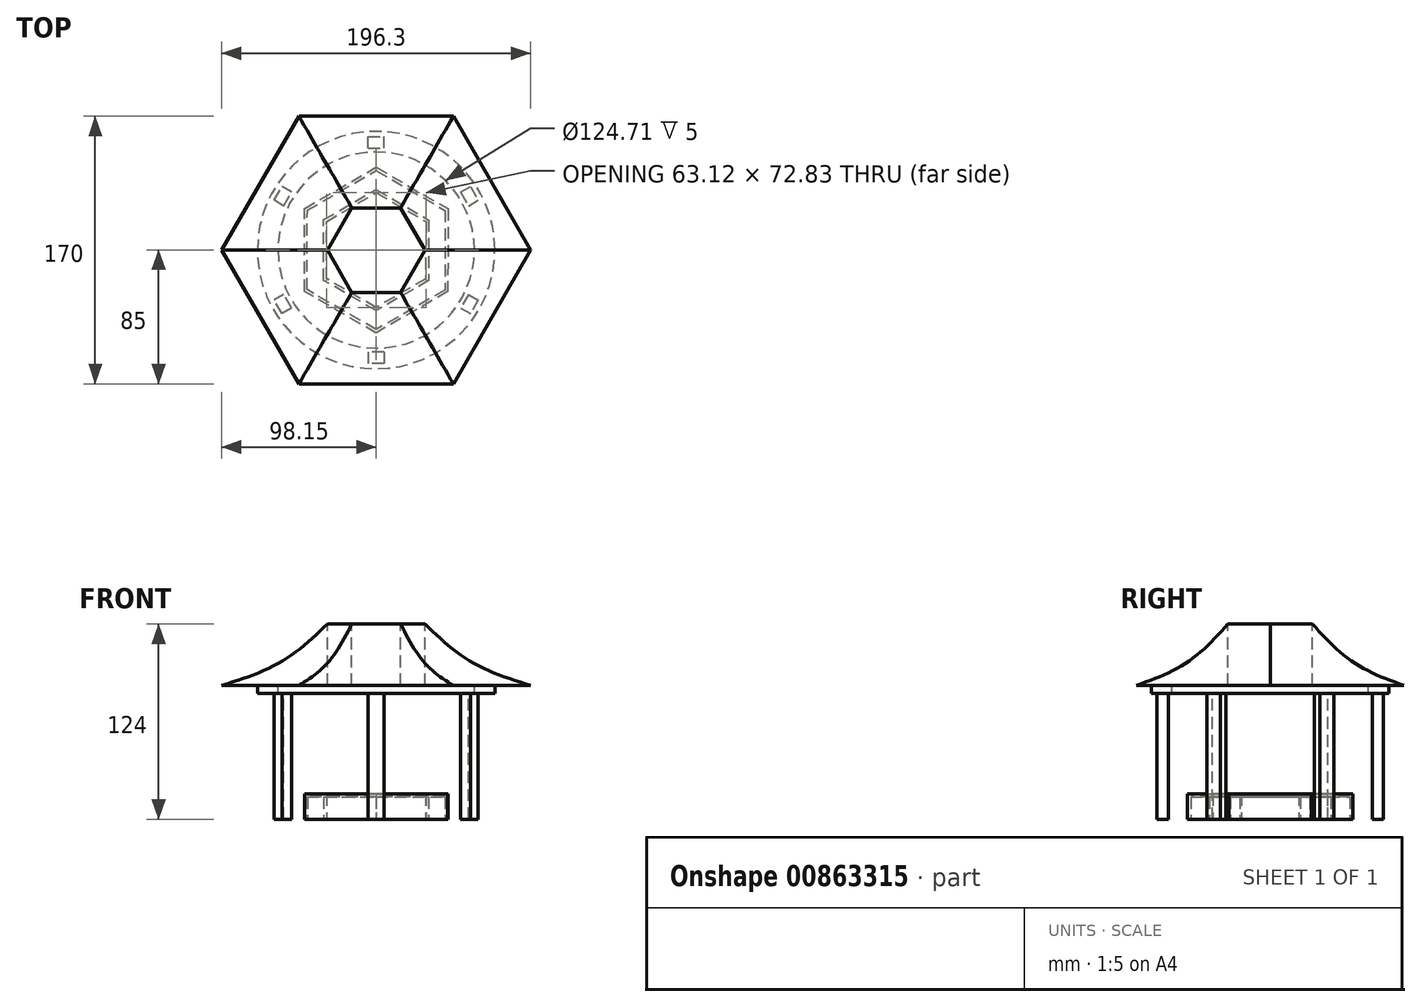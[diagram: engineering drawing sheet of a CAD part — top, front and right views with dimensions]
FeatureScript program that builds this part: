
annotation { "Feature Type Name" : "Feature", "Feature Type Description" : "" }
export const myFeature = defineFeature(function(context is Context, id is Id, definition is map)
    precondition{}
    {
        {
            var Q0;
            Q0=qCreatedBy(makeId("Top.planeOp"),FACE);
            var sketch = newSketch(context, id + "F0", { "sketchPlane" : qUnion([Q0])});
            skCircle(sketch, "E0.cCircle", {"center": v(0, 0) * mm, "radius": 85 * mm, "construction": true});
            skLineSegment(sketch, "E0.0", {"start": v(-49.07, 85) * mm, "end": v(49.07, 85) * mm});
            skLineSegment(sketch, "E0.1", {"start": v(49.07, 85) * mm, "end": v(98.15, 0) * mm});
            skLineSegment(sketch, "E0.2", {"start": v(98.15, 0) * mm, "end": v(49.07, -85) * mm});
            skLineSegment(sketch, "E0.3", {"start": v(49.07, -85) * mm, "end": v(-49.07, -85) * mm});
            skLineSegment(sketch, "E0.4", {"start": v(-49.07, -85) * mm, "end": v(-98.15, 0) * mm});
            skLineSegment(sketch, "E0.5", {"start": v(-98.15, 0) * mm, "end": v(-49.07, 85) * mm});
            skPoint(sketch, "E0.0.midPoint", {"position": v(0, 85) * mm});
            skSolve(sketch);
        }
        {
            var Q0;
            Q0=qCreatedBy(makeId("Top.planeOp"),FACE);
            cPlane(context, id + "F1", {"entities" : qUnion([Q0]), "cplaneType" : CPlaneType.OFFSET, "offset" : 39 * mm, "width" : 150 * mm, "height" : 150 * mm});
        }
        {
            var Q0;
            Q0=qCreatedBy(id+"F1.planeOp",FACE);
            var sketch = newSketch(context, id + "F2", { "sketchPlane" : qUnion([Q0])});
            skLineSegment(sketch, "E1.0", {"start": v(-98.15, 0) * mm, "end": v(-49.07, 85) * mm});
            skLineSegment(sketch, "E1.1", {"start": v(-49.07, 85) * mm, "end": v(49.07, 85) * mm});
            skLineSegment(sketch, "E1.2", {"start": v(49.07, 85) * mm, "end": v(98.15, 0) * mm});
            skLineSegment(sketch, "E1.3", {"start": v(98.15, 0) * mm, "end": v(49.07, -85) * mm});
            skLineSegment(sketch, "E1.4", {"start": v(49.07, -85) * mm, "end": v(-49.07, -85) * mm});
            skLineSegment(sketch, "E1.5", {"start": v(-49.07, -85) * mm, "end": v(-98.15, 0) * mm});
            skLineSegment(sketch, "E2.0", {"start": v(-15.47, -26.8) * mm, "end": v(-30.95, 0) * mm});
            skLineSegment(sketch, "E2.1", {"start": v(-15.47, 26.8) * mm, "end": v(15.47, 26.8) * mm});
            skLineSegment(sketch, "E2.2", {"start": v(15.47, 26.8) * mm, "end": v(30.95, 0) * mm});
            skLineSegment(sketch, "E2.3", {"start": v(-30.95, 0) * mm, "end": v(-15.47, 26.8) * mm});
            skLineSegment(sketch, "E2.4", {"start": v(30.95, 0) * mm, "end": v(15.47, -26.8) * mm});
            skLineSegment(sketch, "E2.5", {"start": v(15.47, -26.8) * mm, "end": v(-15.47, -26.8) * mm});
            skSolve(sketch);
        }
        {
            var Q0;
            Q0=qCreatedBy(makeId("Top.planeOp"),FACE);
            cPlane(context, id + "F3", {"entities" : qUnion([Q0]), "cplaneType" : CPlaneType.OFFSET, "offset" : 15 * mm, "width" : 150 * mm, "height" : 150 * mm});
        }
        {
            var Q0;
            Q0=qCreatedBy(id+"F3.planeOp",FACE);
            var sketch = newSketch(context, id + "F4", { "sketchPlane" : qUnion([Q0])});
            skLineSegment(sketch, "E3.0", {"start": v(-49.07, -85) * mm, "end": v(-98.15, 0) * mm});
            skLineSegment(sketch, "E3.1", {"start": v(-98.15, 0) * mm, "end": v(-49.07, 85) * mm});
            skLineSegment(sketch, "E3.2", {"start": v(-49.07, 85) * mm, "end": v(49.07, 85) * mm});
            skLineSegment(sketch, "E3.3", {"start": v(49.07, 85) * mm, "end": v(98.15, 0) * mm});
            skLineSegment(sketch, "E3.4", {"start": v(98.15, 0) * mm, "end": v(49.07, -85) * mm});
            skLineSegment(sketch, "E3.5", {"start": v(49.07, -85) * mm, "end": v(-49.07, -85) * mm});
            skLineSegment(sketch, "E4.0", {"start": v(-30.14, -52.2) * mm, "end": v(-60.28, 0) * mm});
            skLineSegment(sketch, "E4.1", {"start": v(-30.14, 52.2) * mm, "end": v(30.14, 52.2) * mm});
            skLineSegment(sketch, "E4.2", {"start": v(30.14, 52.2) * mm, "end": v(60.28, 0) * mm});
            skLineSegment(sketch, "E4.3", {"start": v(-60.28, 0) * mm, "end": v(-30.14, 52.2) * mm});
            skLineSegment(sketch, "E4.4", {"start": v(60.28, 0) * mm, "end": v(30.14, -52.2) * mm});
            skLineSegment(sketch, "E4.5", {"start": v(30.14, -52.2) * mm, "end": v(-30.14, -52.2) * mm});
            skSolve(sketch);
        }
        {
            var Q0;
            Q0=makeQuery(id+"F0.imprint","IMPRINT",FACE,{"disambiguationData":[TD([[makeQuery(id+"F0.imprint","IMPRINT",EDGE,{"derivedFrom":sQuery(id+"F0.wireOp",EDGE,"E0.0")}),-1.0]])]});
            var Q1;
            Q1=makeQuery(id+"F4.imprint","IMPRINT",FACE,{"disambiguationData":[TD([[makeQuery(id+"F4.imprint","IMPRINT",EDGE,{"derivedFrom":sQuery(id+"F4.wireOp",EDGE,"E4.0")}),-1.0]])]});
            var Q2;
            Q2=makeQuery(id+"F2.imprint","IMPRINT",FACE,{"disambiguationData":[TD([[makeQuery(id+"F2.imprint","IMPRINT",EDGE,{"derivedFrom":sQuery(id+"F2.wireOp",EDGE,"E2.0")}),-1.0]])]});
            loft(context, id + "F5", {"sheetProfilesArray" : [{ "sheetProfileEntities" : qUnion([Q0]) }, { "sheetProfileEntities" : qUnion([Q1]) }, { "sheetProfileEntities" : qUnion([Q2]) }]});
        }
        {
            var Q0;
            Q0=makeQuery(id+"F5.opLoft","CAP_FACE",FACE,{"disambiguationData":[OSD([makeQuery(id+"F2.imprint","IMPRINT",FACE,{"disambiguationData":[TD([[makeQuery(id+"F2.imprint","IMPRINT",EDGE,{"derivedFrom":sQuery(id+"F2.wireOp",EDGE,"E2.0")}),-1.0]])]})])],"isStart":true});
            extrude(context, id + "F6", {"entities" : qUnion([Q0]), "operationType" : NewBodyOperationType.REMOVE, "oppositeDirection" : true, "depth" : 67 * mm, "offsetDistance" : 25 * mm});
        }
        {
            var Q0;
            Q0=makeQuery(id+"F5.opLoft","CAP_FACE",FACE,{"disambiguationData":[OSD([makeQuery(id+"F0.imprint","IMPRINT",FACE,{"disambiguationData":[TD([[makeQuery(id+"F0.imprint","IMPRINT",EDGE,{"derivedFrom":sQuery(id+"F0.wireOp",EDGE,"E0.0")}),-1.0]])]})])],"isStart":true});
            var sketch = newSketch(context, id + "F7", { "sketchPlane" : qUnion([Q0])});
            skCircle(sketch, "E5", {"center": v(0, 0) * mm, "radius": 75.42 * mm});
            skCircle(sketch, "E6", {"center": v(0, 0) * mm, "radius": 62.35 * mm});
            skSolve(sketch);
        }
        {
            var Q0;
            Q0=makeQuery(id+"F7.imprint","IMPRINT",FACE,{"disambiguationData":[TD([[makeQuery(id+"F7.imprint","IMPRINT",EDGE,{"derivedFrom":sQuery(id+"F7.wireOp",EDGE,"E5")}),1.0]])]});
            extrude(context, id + "F8", {"entities" : qUnion([Q0]), "depth" : 5 * mm, "offsetDistance" : 25 * mm});
        }
        {
            var Q0;
            Q0=makeQuery(id+"F8.opExtrude","CAP_FACE",FACE,{"disambiguationData":[OSD([sQuery(id+"F7.wireOp",EDGE,"E5"),sQuery(id+"F7.wireOp",EDGE,"E6")])],"isStart":false});
            var sketch = newSketch(context, id + "F9", { "sketchPlane" : qUnion([Q0])});
            skLineSegment(sketch, "E7.bottom", {"start": v(5, 64.82) * mm, "end": v(-5, 64.82) * mm});
            skLineSegment(sketch, "E7.top", {"start": v(5, 72) * mm, "end": v(-5, 72) * mm});
            skLineSegment(sketch, "E7.left", {"start": v(5, 64.82) * mm, "end": v(5, 72) * mm});
            skLineSegment(sketch, "E7.right", {"start": v(-5, 64.82) * mm, "end": v(-5, 72) * mm});
            skPoint(sketch, "E7.middle", {"position": v(0, 68.4) * mm});
            skSolve(sketch);
        }
        {
            var Q0;
            Q0=makeQuery(id+"F9.imprint","IMPRINT",FACE,{"disambiguationData":[TD([[makeQuery(id+"F9.imprint","IMPRINT",EDGE,{"derivedFrom":sQuery(id+"F9.wireOp",EDGE,"59YJztIN-KOAp-sr2L-tyLE-rmCy9pHEsv6O")}),1.0]])]});
            var Q1;
            Q1=makeQuery(id+"F9.imprint","IMPRINT",FACE,{"disambiguationData":[TD([[makeQuery(id+"F9.imprint","IMPRINT",EDGE,{"derivedFrom":sQuery(id+"F9.wireOp",EDGE,"E7.bottom")}),-1.0]])]});
            extrude(context, id + "F10", {"entities" : qUnion([Q0, Q1]), "depth" : 80 * mm, "offsetDistance" : 25 * mm});
        }
        {
            var Q0;
            Q0=qCreatedBy(makeId("Right.planeOp"),FACE);
            var sketch = newSketch(context, id + "F11", { "sketchPlane" : qUnion([Q0])});
            skLineSegment(sketch, "E8", {"start": v(0, 0) * mm, "end": v(0, 56.93) * mm, "construction": true});
            skSolve(sketch);
        }
        {
            var Q0;
            Q0=makeQuery(id+"F10.opExtrude","SWEPT_BODY",BODY,{"disambiguationData":[OSD([sQuery(id+"F9.wireOp",EDGE,"59YJztIN-KOAp-sr2L-tyLE-rmCy9pHEsv6O")])]});
            var Q1;
            Q1=makeQuery(id+"F10.opExtrude","SWEPT_BODY",BODY,{"disambiguationData":[OSD([sQuery(id+"F9.wireOp",EDGE,"E7.bottom"),sQuery(id+"F9.wireOp",EDGE,"E7.top"),sQuery(id+"F9.wireOp",EDGE,"E7.left"),sQuery(id+"F9.wireOp",EDGE,"E7.right")])]});
            var Q2;
            Q2=sQuery(id+"F11.wireOp",EDGE,"E8");
            circularPattern(context, id + "F12", {"entities" : qUnion([Q0, Q1]), "axis" : qUnion([Q2]), "angle" : 360 * degree, "instanceCount" : 6, "equalSpace" : true});
        }
        {
            var Q0;
            Q0=qCreatedBy(makeId("Top.planeOp"),FACE);
            cPlane(context, id + "F13", {"entities" : qUnion([Q0]), "cplaneType" : CPlaneType.OFFSET, "offset" : 85 * mm, "oppositeDirection" : true, "width" : 150 * mm, "height" : 150 * mm});
        }
        {
            var Q0;
            Q0=qCreatedBy(id+"F13.planeOp",FACE);
            var sketch = newSketch(context, id + "F14", { "sketchPlane" : qUnion([Q0])});
            skCircle(sketch, "E9.cCircle", {"center": v(0, 0) * mm, "radius": 45.54 * mm, "construction": true});
            skLineSegment(sketch, "E9.0", {"start": v(45.5, -26.35) * mm, "end": v(-0.06, -52.58) * mm});
            skLineSegment(sketch, "E9.1", {"start": v(-0.06, -52.58) * mm, "end": v(-45.57, -26.24) * mm});
            skLineSegment(sketch, "E9.2", {"start": v(-45.57, -26.24) * mm, "end": v(-45.5, 26.35) * mm});
            skLineSegment(sketch, "E9.3", {"start": v(-45.5, 26.35) * mm, "end": v(0.06, 52.58) * mm});
            skLineSegment(sketch, "E9.4", {"start": v(0.06, 52.58) * mm, "end": v(45.57, 26.24) * mm});
            skLineSegment(sketch, "E9.5", {"start": v(45.57, 26.24) * mm, "end": v(45.5, -26.35) * mm});
            skPoint(sketch, "E9.0.midPoint", {"position": v(22.72, -39.46) * mm});
            skLineSegment(sketch, "E10.0", {"start": v(-31.52, 18.25) * mm, "end": v(0.04, 36.42) * mm});
            skLineSegment(sketch, "E10.1", {"start": v(31.56, 18.17) * mm, "end": v(31.52, -18.25) * mm});
            skLineSegment(sketch, "E10.2", {"start": v(31.52, -18.25) * mm, "end": v(-0.04, -36.42) * mm});
            skLineSegment(sketch, "E10.3", {"start": v(0.04, 36.42) * mm, "end": v(31.56, 18.17) * mm});
            skLineSegment(sketch, "E10.4", {"start": v(-0.04, -36.42) * mm, "end": v(-31.56, -18.17) * mm});
            skLineSegment(sketch, "E10.5", {"start": v(-31.56, -18.17) * mm, "end": v(-31.52, 18.25) * mm});
            skSolve(sketch);
        }
        {
            var Q0;
            Q0 = qSketchRegion(id + "F14", true);
            extrude(context, id + "F15", {"entities" : qUnion([Q0]), "depth" : 16 * mm, "offsetDistance" : 25 * mm});
        }
        {
            var Q0;
            Q0=makeQuery(id+"F15.opExtrude","CAP_FACE",FACE,{"disambiguationData":[OSD([sQuery(id+"F14.wireOp",EDGE,"E9.0"),sQuery(id+"F14.wireOp",EDGE,"E9.1"),sQuery(id+"F14.wireOp",EDGE,"E9.2"),sQuery(id+"F14.wireOp",EDGE,"E9.3"),sQuery(id+"F14.wireOp",EDGE,"E9.4"),sQuery(id+"F14.wireOp",EDGE,"E9.5"),sQuery(id+"F14.wireOp",EDGE,"E10.0"),sQuery(id+"F14.wireOp",EDGE,"E10.1"),sQuery(id+"F14.wireOp",EDGE,"E10.2"),sQuery(id+"F14.wireOp",EDGE,"E10.3"),sQuery(id+"F14.wireOp",EDGE,"E10.4"),sQuery(id+"F14.wireOp",EDGE,"E10.5")])],"isStart":true});
            shell(context, id + "F16", {"entities" : qUnion([Q0]), "thickness" : 1.8 * mm});
        }
    });
